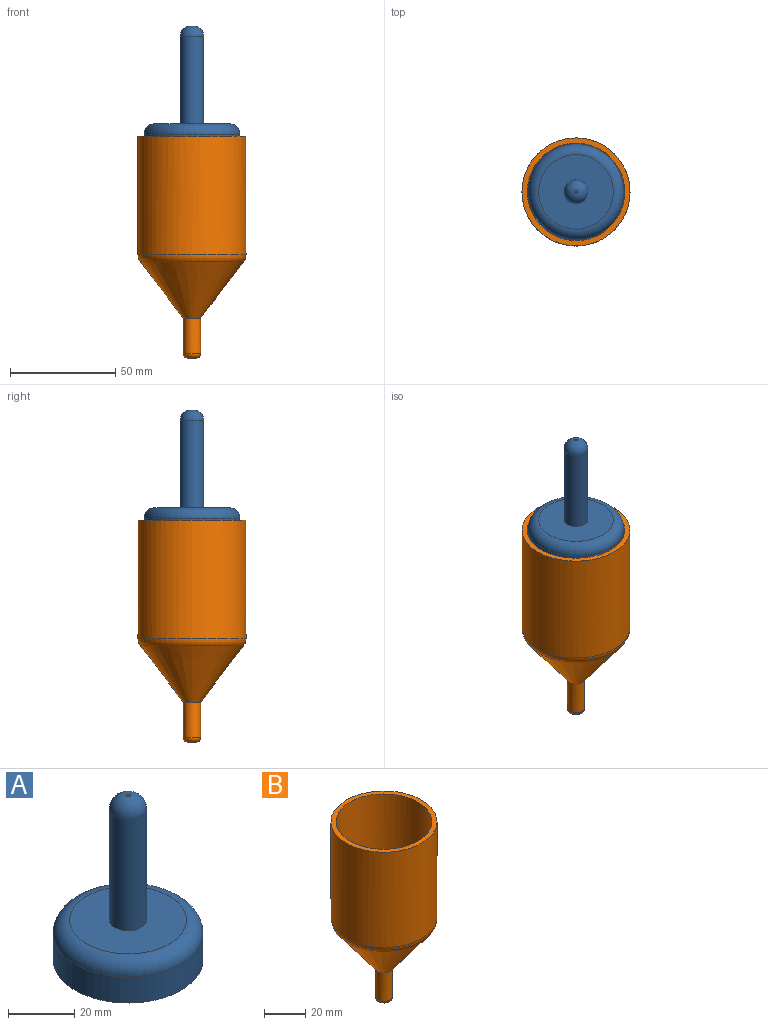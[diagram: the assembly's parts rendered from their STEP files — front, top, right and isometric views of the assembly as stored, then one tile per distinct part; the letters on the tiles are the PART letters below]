
ASSEMBLY  parts=2 mates=1
PART A: 7 faces, bbox 49.1x49.1x61 mm
  f0: cylinder r=22.69mm len=45.38mm, axis (0,0,-1), area 1382.9mm2, adj f2,f6
  f1: plane 35.38x35.38mm, normal (0,0,1), area 883.8mm2, adj f3,f6
  f2: plane 45.38x45.38mm, normal (0,0,-1), area 1617.4mm2, adj f0
  f3: cylinder r=5.62mm len=41.3mm, axis (0,0,-1), area 1459.1mm2, adj f1,f5
  f4: plane 1.25x1.25mm, normal (0,0,1), area 1.2mm2, adj f5
  f5: torus R=0.62mm, axis (0,0,1), area 187.8mm2, adj f3,f4
  f6: torus R=17.69mm, axis (0,0,1), area 1030mm2, adj f0,f1
PART B: 12 faces, bbox 55.4x55.4x105.3 mm
  f0: plane 51.22x51.22mm, normal (0,0,1), area 382.7mm2, adj f4,f10
  f1: plane 4.26x4.26mm, normal (0,0,-1), area 14.3mm2, adj f5
  f2: cylinder r=4.06mm len=16.79mm, axis (0,0,-1), area 428.6mm2, adj f3,f5
  f3: cone r=25.61mm half-angle=37deg, axis (0,0,1), area 3075.2mm2, adj f2,f6
  f4: cylinder r=25.61mm len=56.26mm, axis (0,0,-1), area 9053mm2, adj f0,f6
  f5: torus R=2.13mm, axis (0,0,1), area 64.1mm2, adj f1,f2
  f6: torus R=20.61mm, axis (0,0,1), area 512.4mm2, adj f3,f4
  f7: plane 3.12x3.12mm, normal (0,0,1), area 7.7mm2, adj f8
  f8: cylinder r=1.56mm len=17.06mm, axis (0,0,-1), area 167.4mm2, adj f7,f9
  f9: cone r=23.61mm half-angle=37deg, axis (0,0,1), area 2656.3mm2, adj f8,f11
  f10: cylinder r=23.11mm len=56.26mm, axis (0,0,-1), area 8169.3mm2, adj f0,f11
  f11: torus R=20.61mm, axis (0,0,1), area 232.6mm2, adj f9,f10
PLACE A rot(axis=(0,0,1),55.4deg) t=(-43.83,14.42,-3.03)mm
PLACE B t=(-43.83,14.42,5.78)mm fixed
MATE cylindrical A.f0 <-> B.f2  axis (0,0,-1) through (-43.83,14.42,72.91)mm
